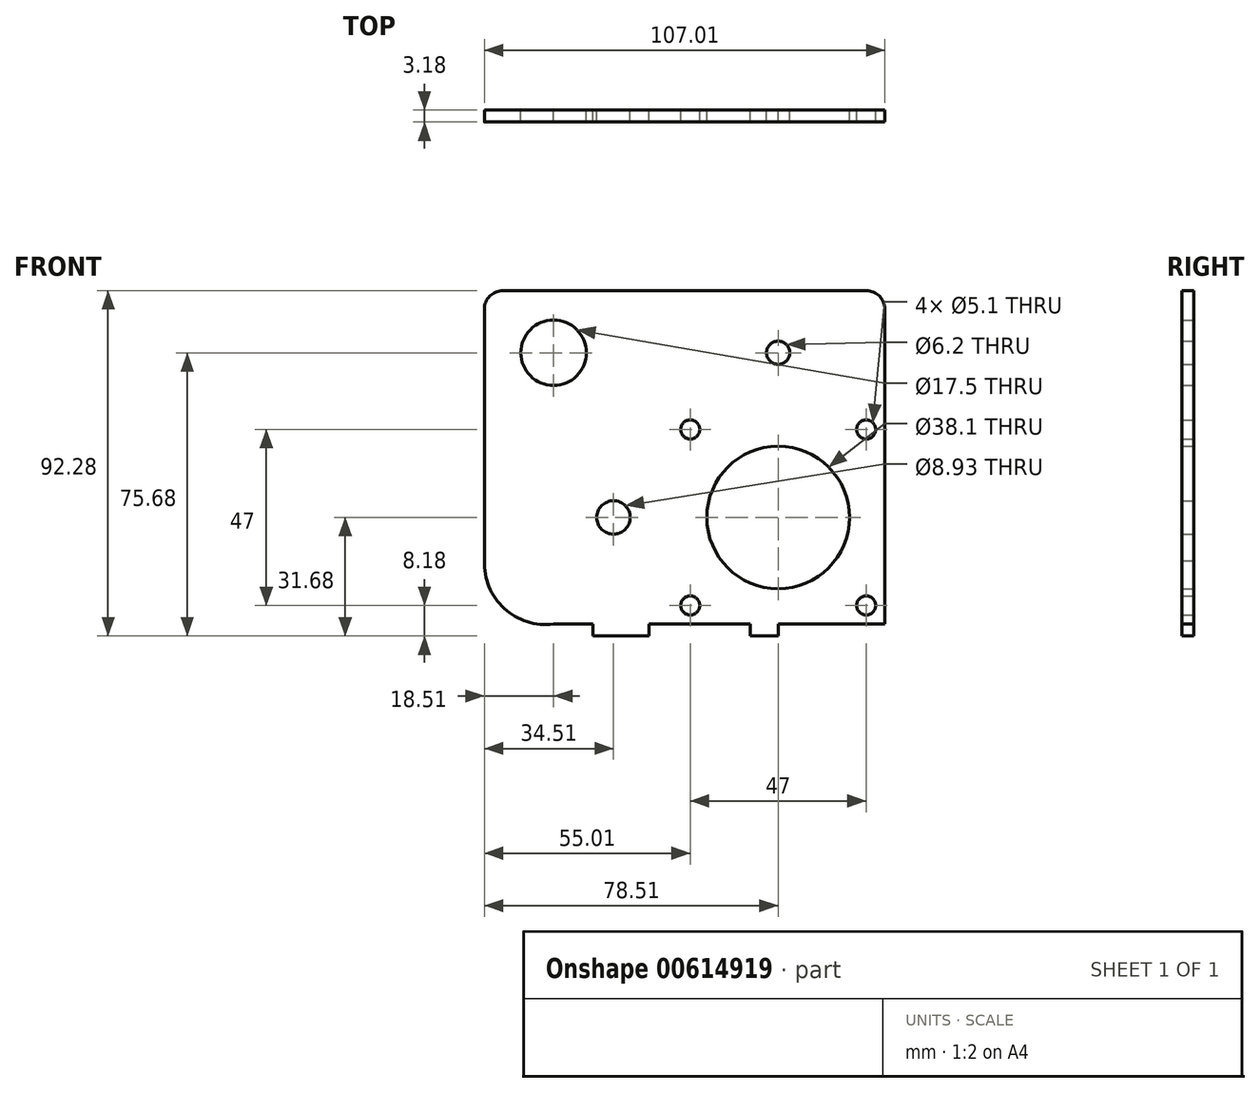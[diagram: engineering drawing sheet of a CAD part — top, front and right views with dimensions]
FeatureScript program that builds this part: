
annotation { "Feature Type Name" : "Feature", "Feature Type Description" : "" }
export const myFeature = defineFeature(function(context is Context, id is Id, definition is map)
    precondition{}
    {
        {
            var Q0;
            Q0=qCreatedBy(makeId("Front.planeOp"),FACE);
            var sketch = newSketch(context, id + "F0", { "sketchPlane" : qUnion([Q0])});
            skLineSegment(sketch, "E0.bottom", {"start": v(-28.5, 28.5) * mm, "end": v(23.5, 28.5) * mm});
            skLineSegment(sketch, "E0.top", {"start": v(-28.5, -28.5) * mm, "end": v(28.5, -28.5) * mm});
            skLineSegment(sketch, "E0.left", {"start": v(-28.5, 28.5) * mm, "end": v(-28.5, -28.5) * mm});
            skLineSegment(sketch, "E0.right", {"start": v(28.5, 23.5) * mm, "end": v(28.5, -28.5) * mm});
            skPoint(sketch, "E0.middle", {"position": v(0, 0) * mm});
            skLineSegment(sketch, "E1.bottom", {"start": v(28.5, -28.5) * mm, "end": v(13.5, -28.5) * mm});
            skLineSegment(sketch, "E1.top", {"start": v(28.5, -31.68) * mm, "end": v(13.5, -31.68) * mm});
            skLineSegment(sketch, "E1.left", {"start": v(28.5, -28.5) * mm, "end": v(28.5, -31.68) * mm});
            skLineSegment(sketch, "E1.right", {"start": v(13.5, -28.5) * mm, "end": v(13.5, -31.67) * mm});
            skLineSegment(sketch, "E2.bottom", {"start": v(-28.5, -28.5) * mm, "end": v(-13.5, -28.5) * mm});
            skLineSegment(sketch, "E2.top", {"start": v(-28.5, -31.67) * mm, "end": v(-13.5, -31.67) * mm});
            skLineSegment(sketch, "E2.left", {"start": v(-28.5, -28.5) * mm, "end": v(-28.5, -31.67) * mm});
            skLineSegment(sketch, "E2.right", {"start": v(-13.5, -28.5) * mm, "end": v(-13.5, -31.67) * mm});
            skLineSegment(sketch, "E3.bottom", {"start": v(0, -28.5) * mm, "end": v(7.5, -28.5) * mm});
            skLineSegment(sketch, "E3.top", {"start": v(0, -31.67) * mm, "end": v(7.5, -31.67) * mm});
            skLineSegment(sketch, "E3.left", {"start": v(0, -28.5) * mm, "end": v(0, -31.67) * mm});
            skLineSegment(sketch, "E3.right", {"start": v(7.5, -28.5) * mm, "end": v(7.5, -31.67) * mm});
            skLineSegment(sketch, "E4.bottom", {"start": v(0, -31.67) * mm, "end": v(-7.5, -31.67) * mm});
            skLineSegment(sketch, "E4.top", {"start": v(0, -28.5) * mm, "end": v(-7.5, -28.5) * mm});
            skLineSegment(sketch, "E4.left", {"start": v(0, -31.67) * mm, "end": v(0, -28.5) * mm});
            skLineSegment(sketch, "E4.right", {"start": v(-7.5, -31.67) * mm, "end": v(-7.5, -28.5) * mm});
            skCircle(sketch, "E5", {"center": v(0, 0) * mm, "radius": 19.05 * mm});
            skLineSegment(sketch, "E6.bottom", {"start": v(-23.5, 23.5) * mm, "end": v(23.5, 23.5) * mm});
            skLineSegment(sketch, "E6.top", {"start": v(-23.5, -23.5) * mm, "end": v(23.5, -23.5) * mm});
            skLineSegment(sketch, "E6.left", {"start": v(-23.5, 23.5) * mm, "end": v(-23.5, -23.5) * mm});
            skLineSegment(sketch, "E6.right", {"start": v(23.5, 23.5) * mm, "end": v(23.5, -23.5) * mm});
            skCircle(sketch, "E7", {"center": v(23.5, 23.5) * mm, "radius": 2.55 * mm});
            skCircle(sketch, "E8.MirrorC", {"center": v(-23.5, 23.5) * mm, "radius": 2.55 * mm});
            skCircle(sketch, "E9.MirrorC", {"center": v(-23.5, -23.5) * mm, "radius": 2.55 * mm});
            skCircle(sketch, "E10.MirrorC", {"center": v(23.5, -23.5) * mm, "radius": 2.55 * mm});
            skPoint(sketch, "E11.visualSharp", {"position": v(28.5, 28.5) * mm});
            skPoint(sketch, "E12.visualSharp", {"position": v(23.5, 28.5) * mm});
            skLineSegment(sketch, "E12.filletArc", {"start": v(23.5, 28.5) * mm, "end": v(23.5, 28.5) * mm});
            skLineSegment(sketch, "E13", {"start": v(23.5, 28.5) * mm, "end": v(28.5, 28.5) * mm});
            skLineSegment(sketch, "E14", {"start": v(28.5, 23.5) * mm, "end": v(28.5, 28.5) * mm});
            skCircle(sketch, "E15", {"center": v(-60, 44) * mm, "radius": 8.75 * mm});
            skPoint(sketch, "E16.visualSharp", {"position": v(-78.5, 28.5) * mm});
            skLineSegment(sketch, "E17", {"start": v(-28.5, -28.5) * mm, "end": v(-34.5, -28.5) * mm});
            skLineSegment(sketch, "E18", {"start": v(-34.5, -28.5) * mm, "end": v(-49.5, -28.5) * mm});
            skLineSegment(sketch, "E19", {"start": v(-49.5, -28.5) * mm, "end": v(-49.5, -31.68) * mm});
            skLineSegment(sketch, "E20", {"start": v(-49.5, -31.67) * mm, "end": v(-34.5, -31.67) * mm});
            skLineSegment(sketch, "E21", {"start": v(-34.5, -31.68) * mm, "end": v(-34.5, -28.5) * mm});
            skLineSegment(sketch, "E22", {"start": v(0, 0) * mm, "end": v(0, 44) * mm});
            skCircle(sketch, "E23", {"center": v(0, 44) * mm, "radius": 3.1 * mm});
            skLineSegment(sketch, "E24.bottom", {"start": v(-28.5, 28.5) * mm, "end": v(28.5, 28.5) * mm});
            skLineSegment(sketch, "E24.top", {"start": v(-28.5, 60.6) * mm, "end": v(23.5, 60.6) * mm});
            skLineSegment(sketch, "E24.left", {"start": v(-28.5, 28.5) * mm, "end": v(-28.5, 60.6) * mm});
            skLineSegment(sketch, "E24.right", {"start": v(28.5, 28.5) * mm, "end": v(28.5, 55.6) * mm});
            skLineSegment(sketch, "E25", {"start": v(-60, 44) * mm, "end": v(-60, -28.5) * mm});
            skLineSegment(sketch, "E26", {"start": v(-60, 44) * mm, "end": v(0, 44) * mm});
            skLineSegment(sketch, "E27", {"start": v(0, 44) * mm, "end": v(0, 44) * mm});
            skLineSegment(sketch, "E28", {"start": v(-28.5, 60.6) * mm, "end": v(-73.5, 60.6) * mm});
            skLineSegment(sketch, "E29", {"start": v(-78.5, 55.6) * mm, "end": v(-78.5, -11.5) * mm});
            skPoint(sketch, "E30.visualSharp", {"position": v(-78.5, 60.6) * mm});
            skArc(sketch, "E30.filletArc", {"start": v(-73.5, 60.6) * mm, "mid": v(-77.04, 59.13) * mm, "end": v(-78.5, 55.6) * mm});
            skArc(sketch, "E31", {"start": v(-78.5, -11.5) * mm, "mid": v(-73.2, -24.29) * mm, "end": v(-60, -28.5) * mm});
            skLineSegment(sketch, "E32", {"start": v(-60, -28.5) * mm, "end": v(-49.5, -28.5) * mm});
            skPoint(sketch, "E33.visualSharp", {"position": v(28.5, 60.6) * mm});
            skArc(sketch, "E33.filletArc", {"start": v(28.5, 55.6) * mm, "mid": v(27.04, 59.13) * mm, "end": v(23.5, 60.6) * mm});
            skLineSegment(sketch, "E34", {"start": v(0, 0) * mm, "end": v(-44, 0) * mm});
            skCircle(sketch, "E35", {"center": v(-44, 0) * mm, "radius": 4.47 * mm});
            skSolve(sketch);
        }
        {
            var Q0;
            Q0=makeQuery(id+"F0.imprint","IMPRINT",FACE,{"disambiguationData":[TD([[makeQuery(id+"F0.imprint","IMPRINT",EDGE,{"derivedFrom":sQuery(id+"F0.wireOp",EDGE,"E5")}),-1.0]])]});
            var Q1;
            Q1=makeQuery(id+"F0.imprint","IMPRINT",FACE,{"disambiguationData":[TD([[makeQuery(id+"F0.imprint","IMPRINT",EDGE,{"derivedFrom":sQuery(id+"F0.wireOp",EDGE,"E1.bottom")}),1.0]])]});
            var Q2;
            Q2=makeQuery(id+"F0.imprint","IMPRINT",FACE,{"disambiguationData":[TD([[makeQuery(id+"F0.imprint","IMPRINT",EDGE,{"derivedFrom":sQuery(id+"F0.wireOp",EDGE,"E3.bottom")}),-1.0]])]});
            var Q3;
            Q3=makeQuery(id+"F0.imprint","IMPRINT",FACE,{"disambiguationData":[TD([[makeQuery(id+"F0.imprint","IMPRINT",EDGE,{"derivedFrom":sQuery(id+"F0.wireOp",EDGE,"E4.bottom")}),-1.0]])]});
            var Q4;
            Q4=makeQuery(id+"F0.imprint","IMPRINT",FACE,{"disambiguationData":[TD([[makeQuery(id+"F0.imprint","IMPRINT",EDGE,{"derivedFrom":sQuery(id+"F0.wireOp",EDGE,"E2.bottom")}),-1.0]])]});
            var Q5;
            Q5=makeQuery(id+"F0.imprint","IMPRINT",FACE,{"disambiguationData":[TD([[makeQuery(id+"F0.imprint","IMPRINT",EDGE,{"derivedFrom":sQuery(id+"F0.wireOp",EDGE,"E0.bottom")}),-1.0]])]});
            var Q6;
            Q6=makeQuery(id+"F0.imprint","IMPRINT",FACE,{"disambiguationData":[TD([[makeQuery(id+"F0.imprint","IMPRINT",EDGE,{"derivedFrom":sQuery(id+"F0.wireOp",EDGE,"E15")}),-1.0]])]});
            var Q7;
            Q7=makeQuery(id+"F0.imprint","IMPRINT",FACE,{"disambiguationData":[TD([[makeQuery(id+"F0.imprint","IMPRINT",EDGE,{"derivedFrom":sQuery(id+"F0.wireOp",EDGE,"E18")}),1.0]])]});
            var Q8;
            {var subQ10=sQuery(id+"F0.wireOp",EDGE,"UBpU5qTn-KrrS-G8ys-hke9-8aA7W8N4lxMn");var subQ11=sQuery(id+"F0.wireOp",EDGE,"E5");var subQ12=makeQuery(id+"F0.imprint","INTERSECT",VERTEX,{"derivedFrom":[subQ11,subQ10]});Q8=makeQuery(id+"F0.imprint","IMPRINT",FACE,{"disambiguationData":[TD([[makeQuery(id+"F0.imprint","IMPRINT",EDGE,{"disambiguationData":[TD([[subQ12,-1.0]])],"derivedFrom":subQ11}),-1.0]])]});}
            var Q9;
            Q9=makeQuery(id+"F0.imprint","IMPRINT",FACE,{"disambiguationData":[TD([[makeQuery(id+"F0.imprint","IMPRINT",EDGE,{"derivedFrom":sQuery(id+"F0.wireOp",EDGE,"E0.right")}),-1.0]])]});
            var Q10;
            {var subQ5=sQuery(id+"F0.wireOp",EDGE,"E8.MirrorC");var subQ6=sQuery(id+"F0.wireOp",EDGE,"E6.bottom");var subQ7=makeQuery(id+"F0.imprint","INTERSECT",VERTEX,{"derivedFrom":[subQ6,subQ5]});Q10=makeQuery(id+"F0.imprint","IMPRINT",FACE,{"disambiguationData":[TD([[makeQuery(id+"F0.imprint","IMPRINT",EDGE,{"disambiguationData":[TD([[subQ7,-1.0]])],"derivedFrom":subQ6}),1.0]])]});}
            var Q11;
            Q11=makeQuery(id+"F0.imprint","IMPRINT",FACE,{"disambiguationData":[TD([[makeQuery(id+"F0.imprint","IMPRINT",EDGE,{"derivedFrom":sQuery(id+"F0.wireOp",EDGE,"E23")}),-1.0]])]});
            var Q12;
            {var subQ0=sQuery(id+"F0.wireOp",EDGE,"E24.top");Q12=makeQuery(id+"F0.imprint","IMPRINT",FACE,{"disambiguationData":[TD([[makeQuery(id+"F0.imprint","IMPRINT",EDGE,{"derivedFrom":subQ0}),-1.0]])]});}
            var Q13;
            {var subQ0=sQuery(id+"F0.wireOp",EDGE,"E17");Q13=makeQuery(id+"F0.imprint","IMPRINT",FACE,{"disambiguationData":[TD([[makeQuery(id+"F0.imprint","IMPRINT",EDGE,{"derivedFrom":subQ0}),-1.0]])]});}
            var Q14;
            {var subQ5=sQuery(id+"F0.wireOp",EDGE,"E22");var subQ16=sQuery(id+"F0.wireOp",EDGE,"E5");var subQ17=makeQuery(id+"F0.imprint","INTERSECT",VERTEX,{"derivedFrom":[subQ16,subQ5]});Q14=makeQuery(id+"F0.imprint","IMPRINT",FACE,{"disambiguationData":[TD([[makeQuery(id+"F0.imprint","IMPRINT",EDGE,{"disambiguationData":[TD([[subQ17,1.0]])],"derivedFrom":subQ16}),-1.0]])]});}
            extrude(context, id + "F1", {"entities" : qUnion([Q0, Q1, Q2, Q3, Q4, Q5, Q6, Q7, Q8, Q9, Q10, Q11, Q12, Q13, Q14]), "depth" : 3.17 * mm, "offsetDistance" : 25 * mm});
        }
    });
